# Revit family: MP-1000_RFA
name_source: partatom
category: Aparatos sanitarios
units: mm (PartAtom-declared; Revit-internal decimal feet)

## family parameters
Activar corte en vistas = No
Compartido = Sí
Corte con vacíos al cargar = No
Cota de conector redondo = Usar diámetro
Mantener orientación de anotación = No
Número OmniClass = 23.45.55.17
Punto de cálculo de habitación = Sí
Se basa en plano de trabajo = Sí
Siempre vertical = Sí
Tipo de pieza = Normal
Título OmniClass = Mixing Faucets

## types (1)
- MP-1000
    Accesorios = Contra de push, Inserto para rebosadero, Herramienta para sujeción, Kit de manteimiento.
    Brass Chromed = Brass
    Cartucho = Valvex a nivel izquierdo Valvex a nivel derecho.
    Comentarios de tipo = Incluye contra de push. Incluye inserto para usarse con lavabos sin rebosadero. Compatible con lavabos de sobreponer (3 orificios), sobrecubierta o bajocubierta.
    Descripción = Mezcladora para lavabo con desagüe de push, instalación de 8" a 12" con valvex a nivel discos ceráicos a ¼ de vuelta izquierda y derecha.
    Elevación por defecto = 1"
    Fabricante = HELVEX
    Imagen de tipo = MP-1000.JPG
    Inlet Threads = ½" - 14 NPSM
    Max. Water Flow = 1.3 gal/min
    Max. Working Pressure = 85.3 psi
    Min. Working Pressure = 14.2 psi
    Modelo = MP-1000
    Operación = Los manerales tienen una rotación de 90° para abrir, cerrar y regular la temperatura del agua.
    Satin = Satín
    Support Base Diameter = 2"
    Total Height = 4"
    Total Length = 12"
    Total Width = 7"
    URL = https://helvex.com.mx

## geometry (parser evidence)
native form markers: Sweep x3
no freeform markers — native parametric forms only
